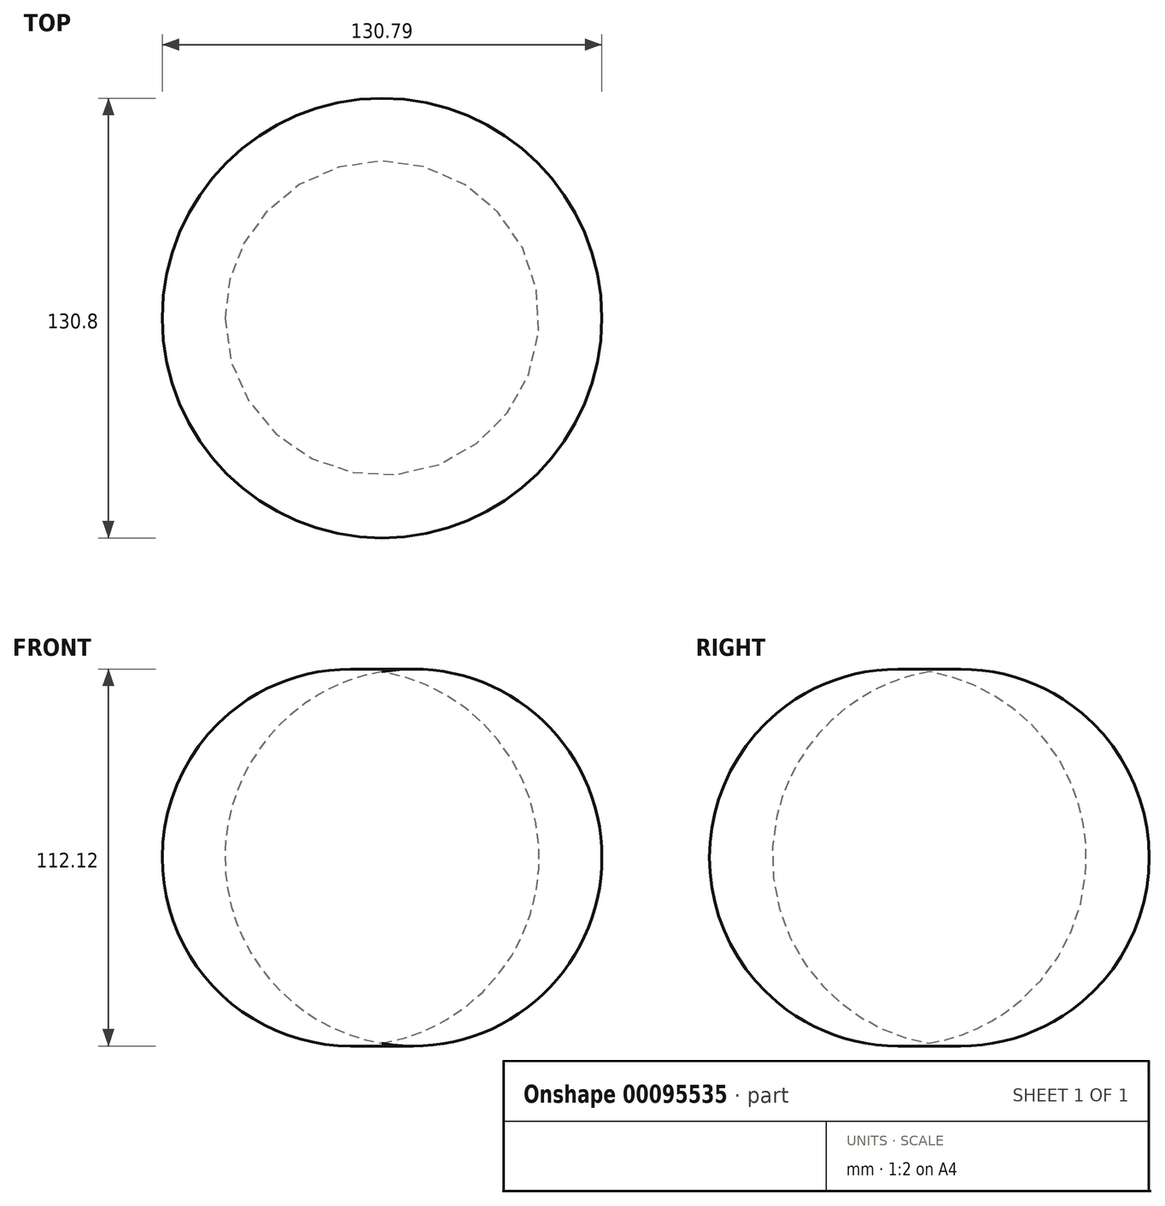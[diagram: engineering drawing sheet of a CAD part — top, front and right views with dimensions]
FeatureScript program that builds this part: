
annotation { "Feature Type Name" : "Feature", "Feature Type Description" : "" }
export const myFeature = defineFeature(function(context is Context, id is Id, definition is map)
    precondition{}
    {
        {
            var Q0;
            Q0=qCreatedBy(makeId("Front.planeOp"),FACE);
            var sketch = newSketch(context, id + "F0", { "sketchPlane" : qUnion([Q0])});
            skLineSegment(sketch, "E0", {"start": v(-51.55, 55.28) * mm, "end": v(-51.55, -55.28) * mm});
            skArc(sketch, "E1", {"start": v(-51.55, -55.28) * mm, "mid": v(13.84, 0) * mm, "end": v(-51.55, 55.28) * mm});
            skSolve(sketch);
        }
        {
            var Q0;
            Q0=makeQuery(id+"F0.imprint","IMPRINT",FACE,{"disambiguationData":[TD([[makeQuery(id+"F0.imprint","IMPRINT",EDGE,{"derivedFrom":sQuery(id+"F0.wireOp",EDGE,"E0")}),1.0]])]});
            var Q1;
            Q1=sQuery(id+"F0.wireOp",EDGE,"E0");
            revolve(context, id + "F1", {"entities" : qUnion([Q0]), "axis" : qUnion([Q1]), "revolveType" : RevolveType.FULL});
        }
    });
